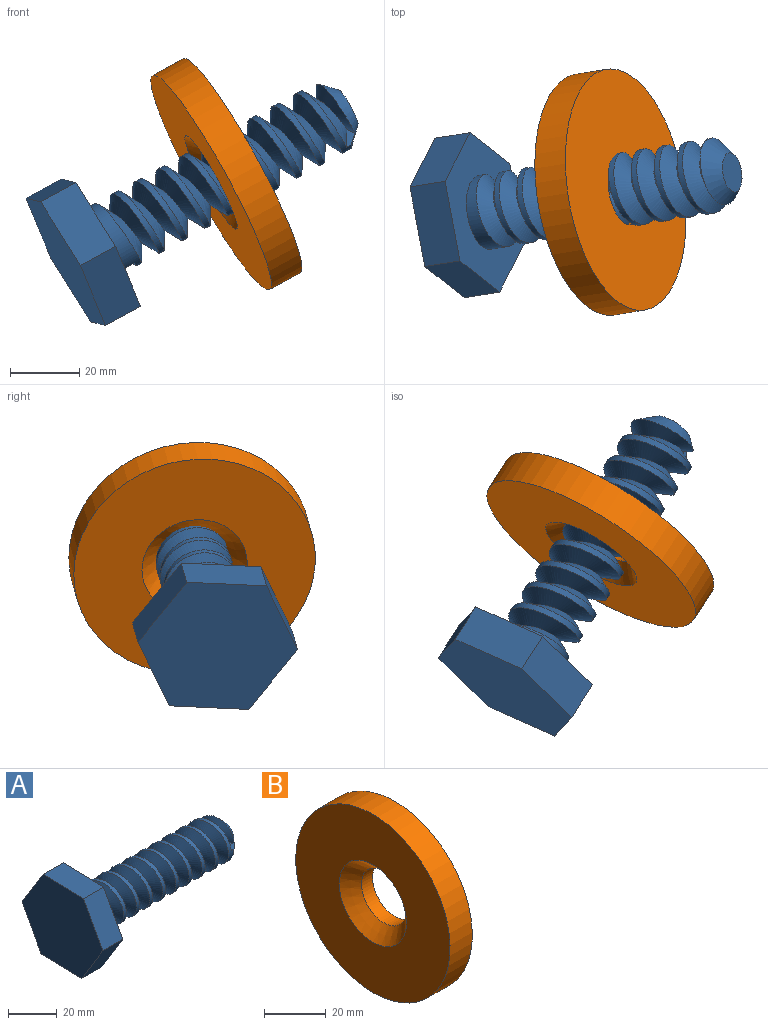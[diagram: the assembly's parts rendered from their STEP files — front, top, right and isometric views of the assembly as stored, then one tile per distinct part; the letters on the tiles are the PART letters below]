
ASSEMBLY  parts=2 mates=1
PART A: 16 faces, bbox 94x46.9x41.2 mm
  f0: cylinder r=10.79mm len=77.22mm, axis (-1,0,0), area 1480.9mm2, adj f1,f8,f11,f12,f13,f15
  f1: cone r=5.71mm half-angle=45deg, axis (-1,0,0), area 305.1mm2, adj f0,f10,f11,f15
  f2: plane 20.61x11.68mm, normal (0,0.88,-0.48), area 274.1mm2, adj f3,f7,f8,f9
  f3: plane 20.01x12.25mm, normal (0,0.85,0.52), area 274.1mm2, adj f2,f4,f8,f9
  f4: plane 23.46x11.68mm, normal (0,-0.03,1), area 274.1mm2, adj f3,f5,f8,f9
  f5: plane 20.61x11.68mm, normal (0,-0.88,0.48), area 274.1mm2, adj f4,f6,f8,f9
  f6: plane 20.01x12.25mm, normal (0,-0.85,-0.52), area 274.1mm2, adj f5,f7,f8,f9
  f7: plane 23.46x11.68mm, normal (0,0.03,-1), area 274.1mm2, adj f2,f6,f8,f9
  f8: plane 46.91x41.22mm, normal (1,0,0), area 1064.2mm2, adj f0,f2,f3,f4,f5,f6,f7,f14
  f9: plane 46.91x41.22mm, normal (-1,0,0), area 1430.3mm2, adj f2,f3,f4,f5,f6,f7
  f10: plane 11.43x11.43mm, normal (1,0,0), area 102.6mm2, adj f1
  f11: plane 5.08x4.29mm, normal (0,0,1), area 9mm2, adj f0,f1,f13,f15
  f12: plane 5.87x5.08mm, normal (0,0,-1), area 14.9mm2, adj f0,f13,f14,f15
  f13: bspline ~79.13x21.59mm, area 3075.2mm2, adj f0,f11,f12,f14,f15
  f14: cylinder r=10.79mm len=4.73mm, axis (-1,0,0), area 1.3mm2, adj f8,f12,f13
  f15: bspline ~79.13x21.59mm, area 2989.6mm2, adj f0,f1,f11,f12,f13
PART B: 5 faces, bbox 10.2x70.5x70.5 mm
  f0: cylinder r=35.26mm len=70.51mm, axis (-1,0,0), area 2250.7mm2, adj f1,f2
  f1: plane 70.51x70.51mm, normal (1,0,0), area 3572.6mm2, adj f0,f3
  f2: plane 70.51x70.51mm, normal (-1,0,0), area 3163.2mm2, adj f0,f4
  f3: cylinder r=10.29mm len=20.57mm, axis (-1,0,0), area 328.3mm2, adj f1,f4
  f4: cone r=10.29mm half-angle=45deg, axis (-1,0,0), area 579mm2, adj f2,f3
PLACE A rot(axis=(0.89,-0.3,0.33),69.7deg) t=(-733.7,40.21,-90.23)mm
PLACE B rot(axis=(0.95,-0.08,0.29),118.5deg) t=(-713.13,102.99,-44.39)mm
MATE cylindrical A.f0 <-> B.f0  axis (0.87,0.14,0.47) through (-652.01,53.29,-45.64)mm
